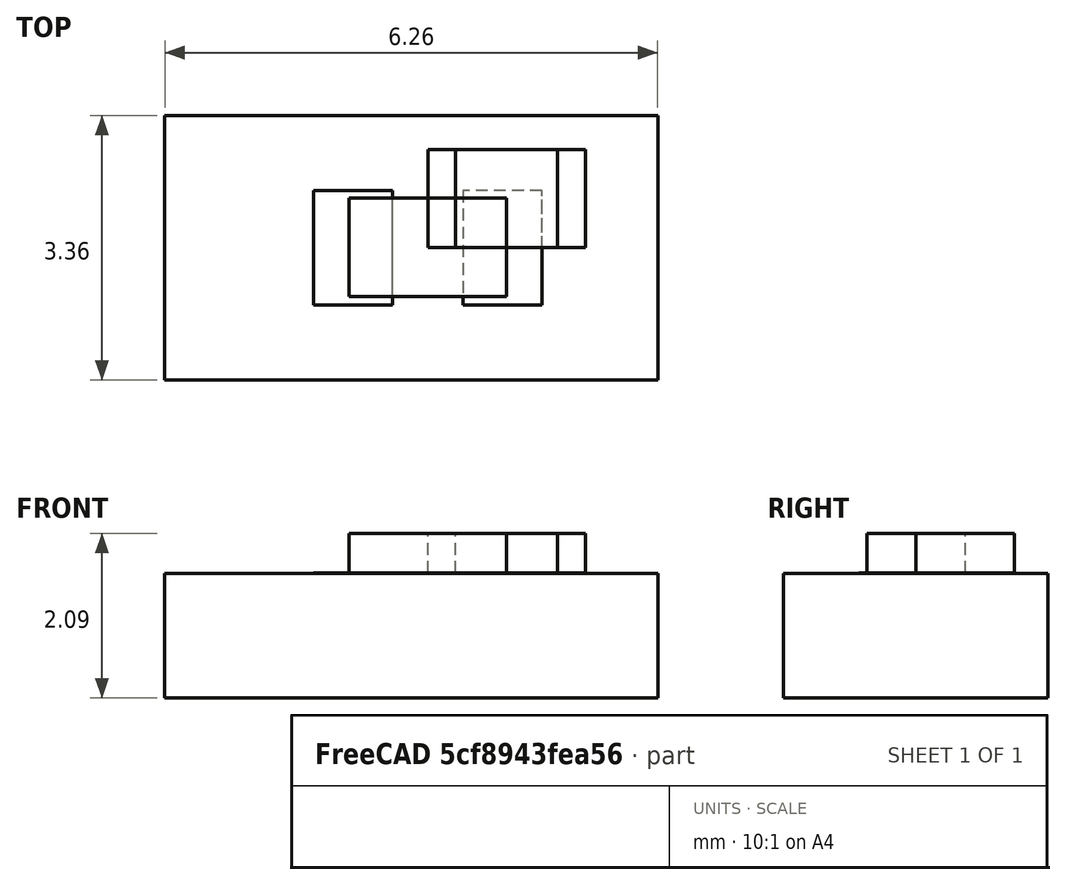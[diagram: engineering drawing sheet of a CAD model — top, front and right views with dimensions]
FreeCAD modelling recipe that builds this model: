
FCSTD DOCUMENT  (FreeCAD 0.17R13541 (Git))
Label: CAPC2012X100N
License: All rights reserved
LicenseURL: http://en.wikipedia.org/wiki/All_rights_reserved
objects: Part::FeaturePython×4, Part::Box×3, App::DocumentObjectGroup×1, Part::Feature×1
note: 8 computed .brp shape members not serialized (recipe doc carries the construction recipe); baked Part::Feature solids carry a one-line shape summary decoded from their .brp

FEATURE [Part::Box] Box  label="pad1"
  AttacherType = Attacher::AttachEngine3D
  Height = 0.5
  Length = 0.35
  Width = 1.25
FEATURE [Part::Box] Box001  label="body"
  AttacherType = Attacher::AttachEngine3D
  Height = 0.5
  Length = 1.3
  Placement = pos=(0.35,0,0) rot=(0,0,1;0rad)
  Width = 1.25
  expr: Length = 2 - 0.34999999999999998 - 0.34999999999999998
FEATURE [Part::Box] Box002  label="pad2"
  AttacherType = Attacher::AttachEngine3D
  Height = 0.5
  Length = 0.35
  Placement = pos=(1.65,0,0) rot=(0,0,1;0rad)
  Width = 1.25
  expr: Placement.Base.x = 2 - 0.34999999999999998
FEATURE [Part::FeaturePython] FCrtYd_lines  label="FCrtYd"  # a2plus imported part (geometry in sourceFile) (typed FeaturePython)
  fixedPosition = true
FEATURE [Part::FeaturePython] Filk_lines  label="FrontSilk"  # a2plus imported part (geometry in sourceFile) (typed FeaturePython)
  fixedPosition = true
FEATURE [Part::FeaturePython] TopPads  # a2plus imported part (geometry in sourceFile) (typed FeaturePython)
  fixedPosition = true
FEATURE [Part::FeaturePython] newPCB  label="Pcb"  # a2plus imported part (geometry in sourceFile) (typed FeaturePython)
  fixedPosition = true
FEATURE [App::DocumentObjectGroup] CAPCP2012X100N_fp  label="CAPC2012X100N_fp"
  Group = -> [FCrtYd_lines,Filk_lines,TopPads,newPCB]
FEATURE [Part::Feature] Shape001  label="CAPC2012X100N"
  shape: bbox 2 x 1.25 x 0.5 mm, 14 faces (baked)
